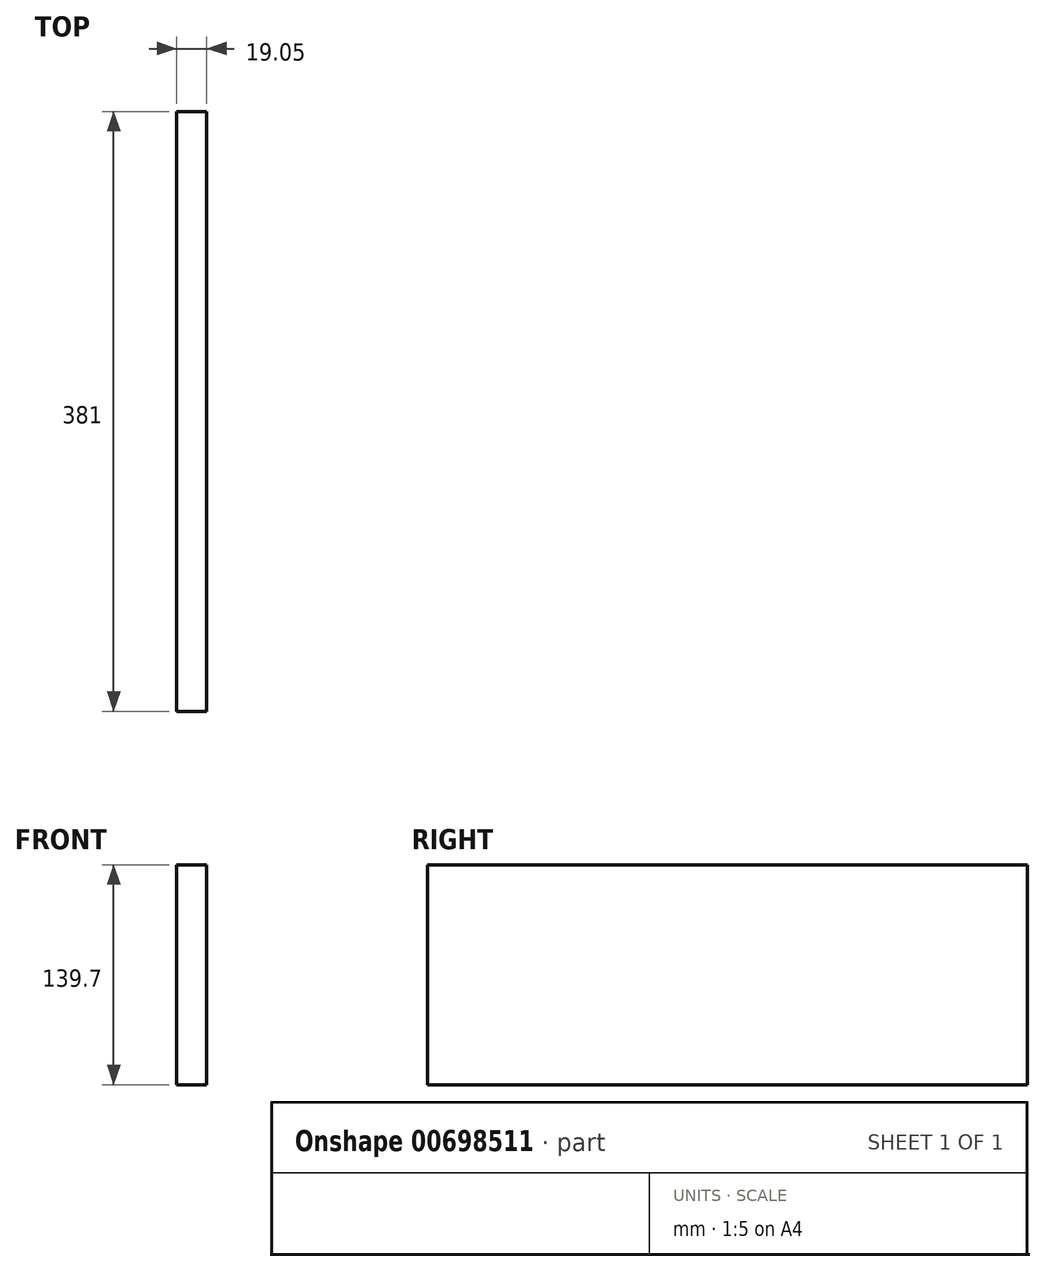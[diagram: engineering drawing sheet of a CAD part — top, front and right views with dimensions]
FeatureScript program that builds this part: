
annotation { "Feature Type Name" : "Feature", "Feature Type Description" : "" }
export const myFeature = defineFeature(function(context is Context, id is Id, definition is map)
    precondition{}
    {
        {
            var Q0;
            Q0=qCreatedBy(makeId("Right.planeOp"),FACE);
            var sketch = newSketch(context, id + "F0", { "sketchPlane" : qUnion([Q0])});
            skLineSegment(sketch, "E0.bottom", {"start": v(-306.01, 189.06) * mm, "end": v(74.99, 189.06) * mm});
            skLineSegment(sketch, "E0.top", {"start": v(-306.01, 49.36) * mm, "end": v(74.99, 49.36) * mm});
            skLineSegment(sketch, "E0.left", {"start": v(-306.01, 189.06) * mm, "end": v(-306.01, 49.36) * mm});
            skLineSegment(sketch, "E0.right", {"start": v(74.99, 189.06) * mm, "end": v(74.99, 49.36) * mm});
            skSolve(sketch);
        }
        {
            var Q0;
            Q0 = qSketchRegion(id + "F0", true);
            extrude(context, id + "F1", {"entities" : qUnion([Q0]), "depth" : 19.05 * mm, "offsetDistance" : 25.4 * mm});
        }
    });
